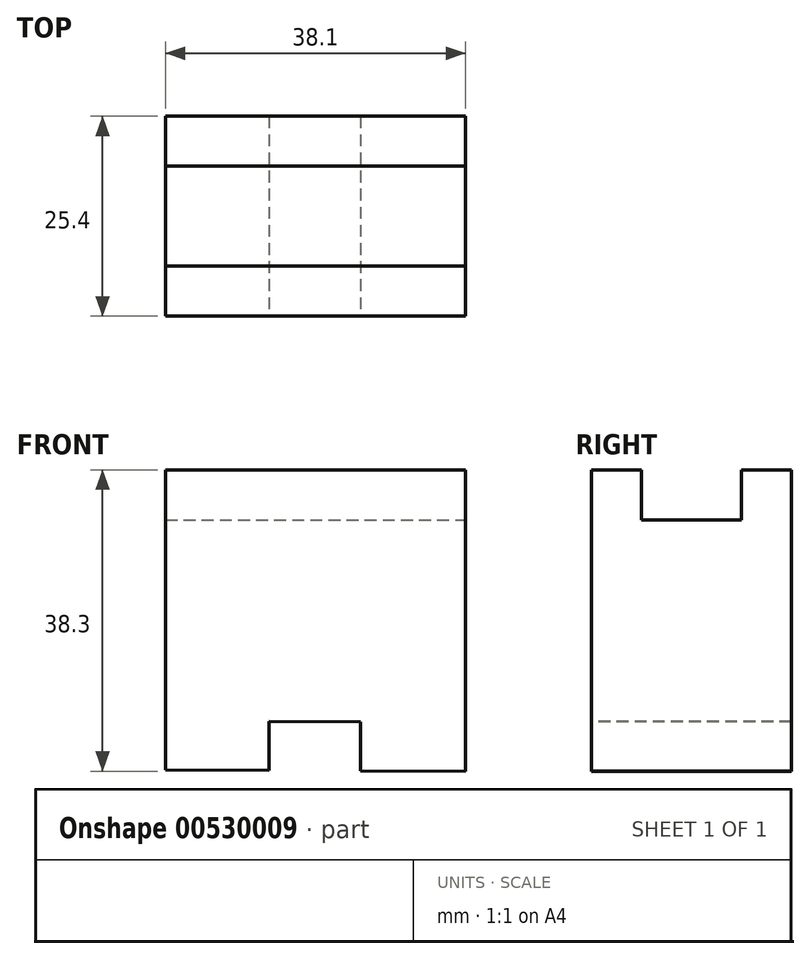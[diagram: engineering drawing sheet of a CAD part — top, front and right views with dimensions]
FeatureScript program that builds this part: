
annotation { "Feature Type Name" : "Feature", "Feature Type Description" : "" }
export const myFeature = defineFeature(function(context is Context, id is Id, definition is map)
    precondition{}
    {
        {
            var Q0;
            Q0=qCreatedBy(makeId("Front.planeOp"),FACE);
            var sketch = newSketch(context, id + "F0", { "sketchPlane" : qUnion([Q0])});
            skLineSegment(sketch, "E0", {"start": v(-60.54, 65.23) * mm, "end": v(-60.54, 27.13) * mm});
            skLineSegment(sketch, "E1", {"start": v(-60.54, 65.23) * mm, "end": v(-22.44, 65.23) * mm});
            skLineSegment(sketch, "E2", {"start": v(-22.44, 65.23) * mm, "end": v(-22.44, 26.93) * mm});
            skLineSegment(sketch, "E3", {"start": v(-60.54, 27.13) * mm, "end": v(-22.44, 26.93) * mm});
            skSolve(sketch);
        }
        {
            var Q0;
            Q0=makeQuery(id+"F0.imprint","IMPRINT",FACE,{"disambiguationData":[TD([[makeQuery(id+"F0.imprint","IMPRINT",EDGE,{"derivedFrom":sQuery(id+"F0.wireOp",EDGE,"E0")}),1.0]])]});
            extrude(context, id + "F1", {"entities" : qUnion([Q0]), "depth" : 25.4 * mm, "offsetDistance" : 25.4 * mm});
        }
        {
            var Q0;
            Q0=makeQuery(id+"F1.opExtrude","CAP_FACE",FACE,{"disambiguationData":[OSD([sQuery(id+"F0.wireOp",EDGE,"E0"),sQuery(id+"F0.wireOp",EDGE,"E1"),sQuery(id+"F0.wireOp",EDGE,"E2"),sQuery(id+"F0.wireOp",EDGE,"E3")])],"isStart":false});
            var sketch = newSketch(context, id + "F2", { "sketchPlane" : qUnion([Q0])});
            skLineSegment(sketch, "E4", {"start": v(-47.41, 27.06) * mm, "end": v(-47.38, 33.4) * mm});
            skLineSegment(sketch, "E5", {"start": v(-47.38, 33.4) * mm, "end": v(-35.76, 33.35) * mm});
            skLineSegment(sketch, "E6", {"start": v(-35.76, 33.35) * mm, "end": v(-35.76, 27) * mm});
            skLineSegment(sketch, "E7", {"start": v(-60.54, 33.35) * mm, "end": v(-22.44, 33.14) * mm});
            skSolve(sketch);
        }
        {
            var Q0;
            {var subQ0=sQuery(id+"F2.wireOp",EDGE,"E4");var subQ1=makeQuery(id+"F1.opExtrude","CAP_EDGE",EDGE,{"disambiguationData":[OSD([sQuery(id+"F0.wireOp",EDGE,"E3")])],"isStart":false});var subQ2=makeQuery(id+"F2.imprint","INTERSECT",VERTEX,{"derivedFrom":[subQ1,subQ0]});Q0=makeQuery(id+"F2.imprint","IMPRINT",FACE,{"disambiguationData":[TD([[makeQuery(id+"F2.imprint","IMPRINT",EDGE,{"disambiguationData":[TD([[subQ2,-1.0]])],"derivedFrom":subQ0}),-1.0]])]});}
            extrude(context, id + "F3", {"entities" : qUnion([Q0]), "operationType" : NewBodyOperationType.REMOVE, "oppositeDirection" : true, "depth" : 25.4 * mm, "offsetDistance" : 25.4 * mm});
        }
        {
            var Q0;
            Q0=makeQuery(id+"F1.opExtrude","SWEPT_FACE",FACE,{"disambiguationData":[OSD([sQuery(id+"F0.wireOp",EDGE,"E2")])]});
            var sketch = newSketch(context, id + "F4", { "sketchPlane" : qUnion([Q0])});
            skLineSegment(sketch, "E8", {"start": v(-19.05, 65.23) * mm, "end": v(-19.05, 58.87) * mm});
            skLineSegment(sketch, "E9", {"start": v(-19.05, 58.87) * mm, "end": v(-6.35, 58.87) * mm});
            skLineSegment(sketch, "E10", {"start": v(-6.35, 58.87) * mm, "end": v(-6.35, 65.23) * mm});
            skLineSegment(sketch, "E11", {"start": v(-19.05, 58.87) * mm, "end": v(-25.4, 58.87) * mm});
            skLineSegment(sketch, "E12", {"start": v(-6.35, 58.87) * mm, "end": v(0, 58.87) * mm});
            skSolve(sketch);
        }
        {
            var Q0;
            {var subQ0=sQuery(id+"F4.wireOp",EDGE,"E8");Q0=makeQuery(id+"F4.imprint","IMPRINT",FACE,{"disambiguationData":[TD([[makeQuery(id+"F4.imprint","IMPRINT",EDGE,{"derivedFrom":subQ0}),1.0]])]});}
            extrude(context, id + "F5", {"entities" : qUnion([Q0]), "operationType" : NewBodyOperationType.REMOVE, "oppositeDirection" : true, "depth" : 38.1 * mm, "offsetDistance" : 25.4 * mm});
        }
    });
